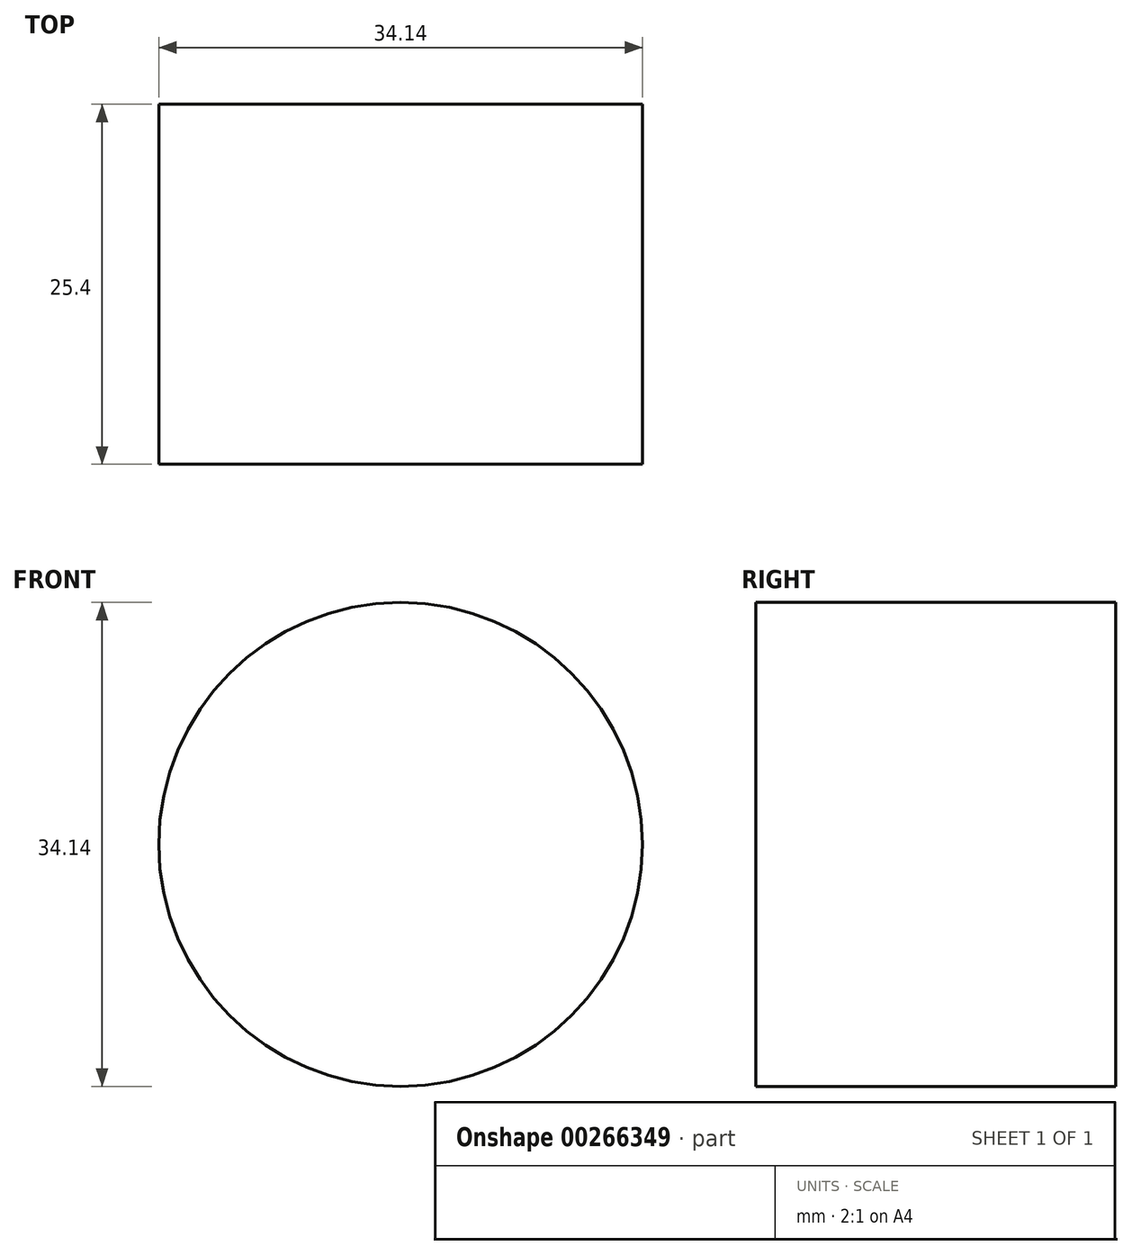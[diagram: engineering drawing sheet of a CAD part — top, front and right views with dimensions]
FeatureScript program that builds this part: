
annotation { "Feature Type Name" : "Feature", "Feature Type Description" : "" }
export const myFeature = defineFeature(function(context is Context, id is Id, definition is map)
    precondition{}
    {
        {
            var Q0;
            Q0=qCreatedBy(makeId("Front.planeOp"),FACE);
            var sketch = newSketch(context, id + "F0", { "sketchPlane" : qUnion([Q0])});
            skCircle(sketch, "E0", {"center": v(0, 0) * mm, "radius": 17.07 * mm});
            skSolve(sketch);
        }
        {
            var Q0;
            Q0 = qSketchRegion(id + "F0", true);
            extrude(context, id + "F1", {"entities" : qUnion([Q0]), "depth" : 25.4 * mm});
        }
    });
